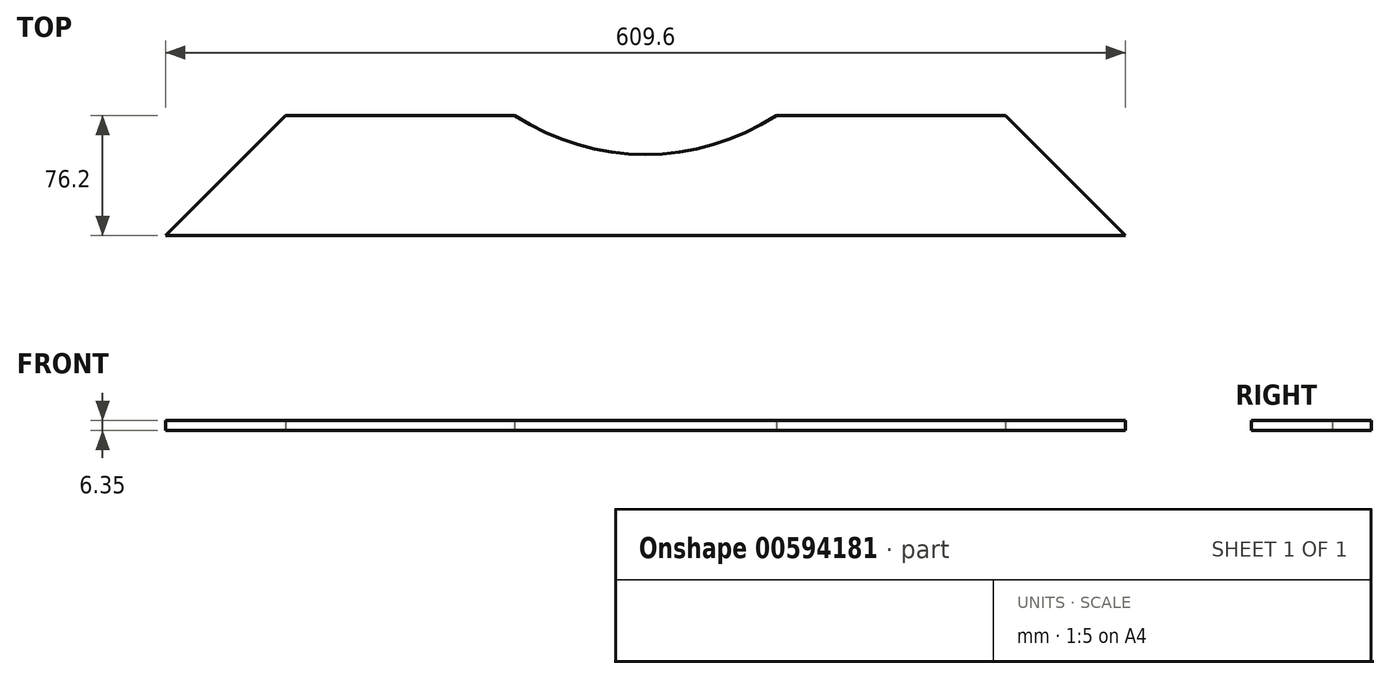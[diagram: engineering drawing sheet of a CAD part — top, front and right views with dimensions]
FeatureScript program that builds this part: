
annotation { "Feature Type Name" : "Feature", "Feature Type Description" : "" }
export const myFeature = defineFeature(function(context is Context, id is Id, definition is map)
    precondition{}
    {
        {
            var Q0;
            Q0=qCreatedBy(makeId("Top.planeOp"),FACE);
            var sketch = newSketch(context, id + "F0", { "sketchPlane" : qUnion([Q0])});
            skLineSegment(sketch, "E0.bottom", {"start": v(0, 0) * mm, "end": v(609.6, 0) * mm});
            skLineSegment(sketch, "E0.top", {"start": v(76.2, 76.2) * mm, "end": v(221.71, 76.2) * mm});
            skLineSegment(sketch, "E0.left", {"start": v(0, 0) * mm, "end": v(0, 0) * mm});
            skLineSegment(sketch, "E0.right", {"start": v(609.6, 0) * mm, "end": v(609.6, 0) * mm});
            skArc(sketch, "E1", {"start": v(221.71, 76.2) * mm, "mid": v(304.8, 51.44) * mm, "end": v(387.89, 76.2) * mm});
            skPoint(sketch, "E1.centerSnap0", {"position": v(304.8, 76.2) * mm});
            skLineSegment(sketch, "E2.trimOffspring", {"start": v(387.89, 76.2) * mm, "end": v(533.4, 76.2) * mm});
            skLineSegment(sketch, "E3", {"start": v(0, 0) * mm, "end": v(76.2, 76.2) * mm});
            skPoint(sketch, "E4.orphan", {"position": v(0, 76.2) * mm});
            skLineSegment(sketch, "E5", {"start": v(533.4, 76.2) * mm, "end": v(609.6, 0) * mm});
            skPoint(sketch, "E6.orphan", {"position": v(609.6, 76.2) * mm});
            skSolve(sketch);
        }
        {
            var Q0;
            Q0=makeQuery(id+"F0.imprint","IMPRINT",FACE,{"disambiguationData":[TD([[makeQuery(id+"F0.imprint","IMPRINT",EDGE,{"derivedFrom":sQuery(id+"F0.wireOp",EDGE,"E0.bottom")}),1.0]])]});
            extrude(context, id + "F1", {"entities" : qUnion([Q0]), "depth" : 6.35 * mm, "offsetDistance" : 25.4 * mm});
        }
    });
